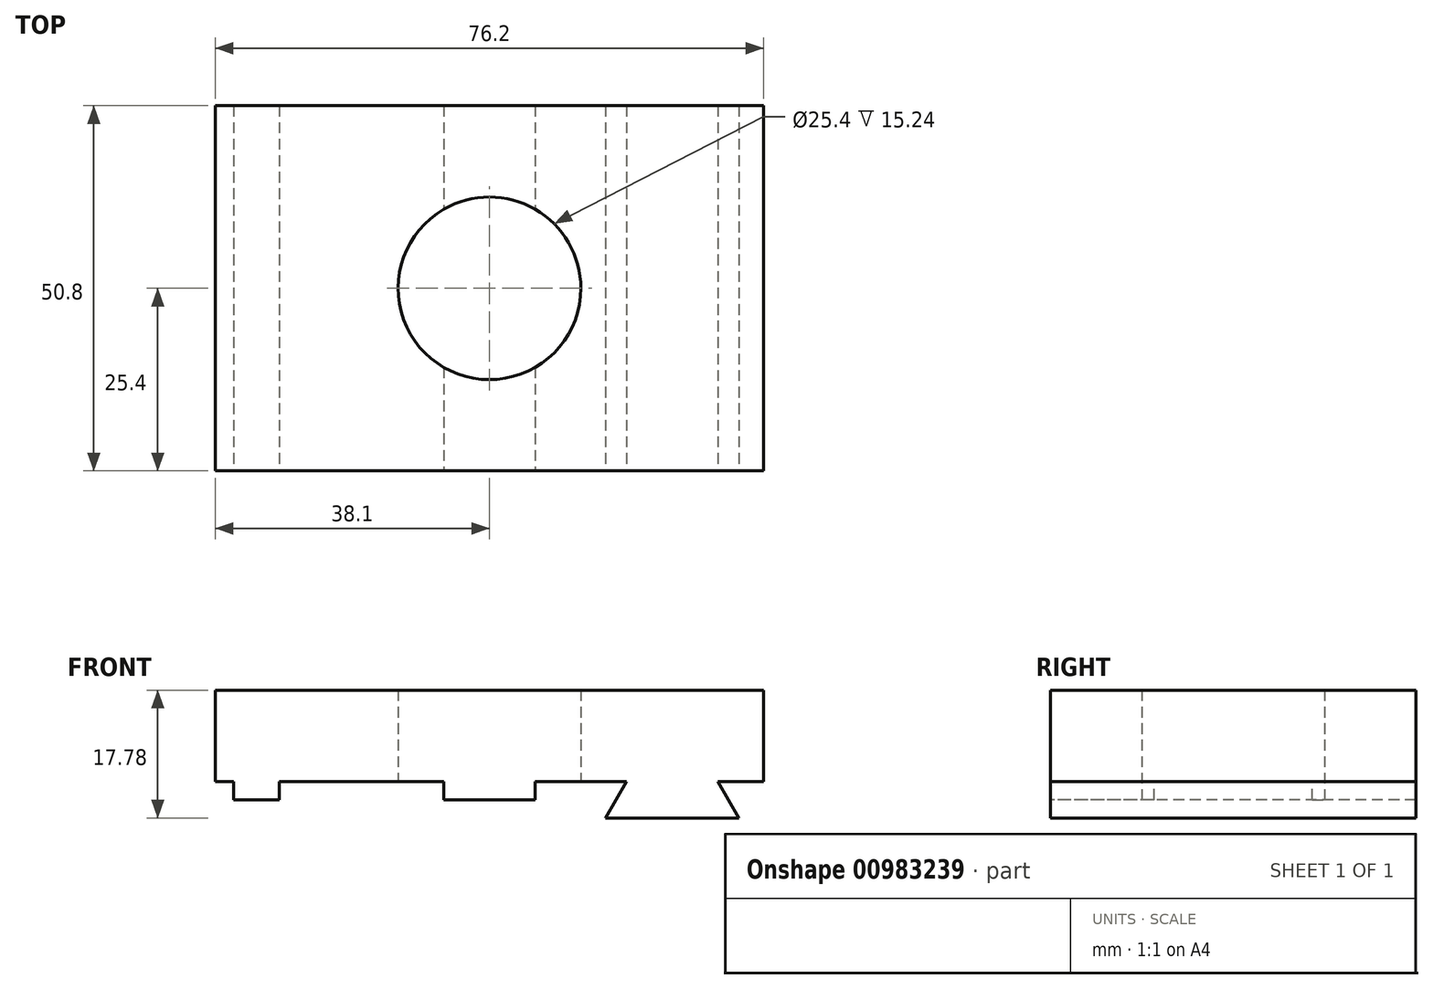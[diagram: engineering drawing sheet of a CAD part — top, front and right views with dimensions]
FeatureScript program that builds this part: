
annotation { "Feature Type Name" : "Feature", "Feature Type Description" : "" }
export const myFeature = defineFeature(function(context is Context, id is Id, definition is map)
    precondition{}
    {
        {
            var Q0;
            Q0=qCreatedBy(makeId("Top.planeOp"),FACE);
            var sketch = newSketch(context, id + "F0", { "sketchPlane" : qUnion([Q0])});
            skLineSegment(sketch, "E0.bottom", {"start": v(-38.1, 25.4) * mm, "end": v(38.1, 25.4) * mm});
            skLineSegment(sketch, "E0.top", {"start": v(-38.1, -25.4) * mm, "end": v(38.1, -25.4) * mm});
            skLineSegment(sketch, "E0.left", {"start": v(-38.1, 25.4) * mm, "end": v(-38.1, -25.4) * mm});
            skLineSegment(sketch, "E0.right", {"start": v(38.1, 25.4) * mm, "end": v(38.1, -25.4) * mm});
            skPoint(sketch, "E0.middle", {"position": v(0, 0) * mm});
            skCircle(sketch, "E1", {"center": v(0, 0) * mm, "radius": 12.7 * mm});
            skSolve(sketch);
        }
        {
            var Q0;
            Q0=makeQuery(id+"F0.imprint","IMPRINT",FACE,{"disambiguationData":[TD([[makeQuery(id+"F0.imprint","IMPRINT",EDGE,{"derivedFrom":sQuery(id+"F0.wireOp",EDGE,"E0.bottom")}),-1.0]])]});
            extrude(context, id + "F1", {"entities" : qUnion([Q0]), "depth" : 12.7 * mm, "offsetDistance" : 25.4 * mm});
        }
        {
            var Q0;
            Q0=makeQuery(id+"F1.opExtrude","CAP_FACE",FACE,{"disambiguationData":[OSD([sQuery(id+"F0.wireOp",EDGE,"E0.bottom"),sQuery(id+"F0.wireOp",EDGE,"E0.top"),sQuery(id+"F0.wireOp",EDGE,"E0.left"),sQuery(id+"F0.wireOp",EDGE,"E0.right"),sQuery(id+"F0.wireOp",EDGE,"E1")])],"isStart":false});
            var sketch = newSketch(context, id + "F2", { "sketchPlane" : qUnion([Q0])});
            skLineSegment(sketch, "E2.bottom", {"start": v(-35.56, 25.4) * mm, "end": v(-29.21, 25.4) * mm});
            skLineSegment(sketch, "E2.top", {"start": v(-35.56, -25.4) * mm, "end": v(-29.21, -25.4) * mm});
            skLineSegment(sketch, "E2.left", {"start": v(-35.56, 25.4) * mm, "end": v(-35.56, -25.4) * mm});
            skLineSegment(sketch, "E2.right", {"start": v(-29.21, 25.4) * mm, "end": v(-29.21, -25.4) * mm});
            skLineSegment(sketch, "E3.bottom", {"start": v(-6.35, 25.4) * mm, "end": v(6.35, 25.4) * mm});
            skLineSegment(sketch, "E3.top", {"start": v(-6.35, -25.4) * mm, "end": v(6.35, -25.4) * mm});
            skLineSegment(sketch, "E3.left", {"start": v(-6.35, 25.4) * mm, "end": v(-6.35, -25.4) * mm});
            skLineSegment(sketch, "E3.right", {"start": v(6.35, 25.4) * mm, "end": v(6.35, -25.4) * mm});
            skPoint(sketch, "E4", {"position": v(0, 0) * mm});
            skPoint(sketch, "E5", {"position": v(0, 25.4) * mm});
            skPoint(sketch, "E6", {"position": v(0, -25.4) * mm});
            skPoint(sketch, "E7.MirrorP", {"position": v(0, 76.2) * mm});
            skSolve(sketch);
        }
        {
            var Q0;
            Q0=makeQuery(id+"F2.imprint","IMPRINT",FACE,{"disambiguationData":[TD([[makeQuery(id+"F2.imprint","IMPRINT",EDGE,{"derivedFrom":sQuery(id+"F2.wireOp",EDGE,"E2.bottom")}),-1.0]])]});
            var Q1;
            {var subQ0=sQuery(id+"F2.wireOp",EDGE,"E3.top");Q1=makeQuery(id+"F2.imprint","IMPRINT",FACE,{"disambiguationData":[TD([[makeQuery(id+"F2.imprint","IMPRINT",EDGE,{"derivedFrom":subQ0}),1.0]])]});}
            var Q2;
            {var subQ0=sQuery(id+"F2.wireOp",EDGE,"E3.bottom");Q2=makeQuery(id+"F2.imprint","IMPRINT",FACE,{"disambiguationData":[TD([[makeQuery(id+"F2.imprint","IMPRINT",EDGE,{"derivedFrom":subQ0}),-1.0]])]});}
            extrude(context, id + "F3", {"entities" : qUnion([Q0, Q1, Q2]), "operationType" : NewBodyOperationType.ADD, "oppositeDirection" : true, "depth" : 15.24 * mm, "offsetDistance" : 25.4 * mm});
        }
        {
            var Q0;
            Q0=makeQuery(id+"F3.boolean.opBoolean","MERGE",FACE,{"derivedFrom":[makeQuery(id+"F1.opExtrude","SWEPT_FACE",FACE,{"disambiguationData":[OSD([sQuery(id+"F0.wireOp",EDGE,"E0.top")])]}),makeQuery(id+"F3.opExtrude","SWEPT_FACE",FACE,{"disambiguationData":[OSD([sQuery(id+"F2.wireOp",EDGE,"E2.top")])]}),makeQuery(id+"F3.opExtrude","SWEPT_FACE",FACE,{"disambiguationData":[OSD([sQuery(id+"F2.wireOp",EDGE,"E3.top")])]})]});
            var sketch = newSketch(context, id + "F4", { "sketchPlane" : qUnion([Q0])});
            skLineSegment(sketch, "E8", {"start": v(19.05, 0) * mm, "end": v(16.12, -5.08) * mm});
            skLineSegment(sketch, "E9", {"start": v(16.12, -5.08) * mm, "end": v(34.68, -5.08) * mm});
            skLineSegment(sketch, "E10", {"start": v(34.68, -5.08) * mm, "end": v(31.75, 0) * mm});
            skLineSegment(sketch, "E11", {"start": v(25.4, -5.08) * mm, "end": v(25.4, 0) * mm, "construction": true});
            skSolve(sketch);
        }
        {
            var Q0;
            {var subQ0=sQuery(id+"F4.wireOp",EDGE,"E8");Q0=makeQuery(id+"F4.imprint","IMPRINT",FACE,{"disambiguationData":[TD([[makeQuery(id+"F4.imprint","IMPRINT",EDGE,{"derivedFrom":subQ0}),1.0]])]});}
            extrude(context, id + "F5", {"entities" : qUnion([Q0]), "operationType" : NewBodyOperationType.ADD, "oppositeDirection" : true, "depth" : 50.8 * mm, "offsetDistance" : 25.4 * mm});
        }
    });
